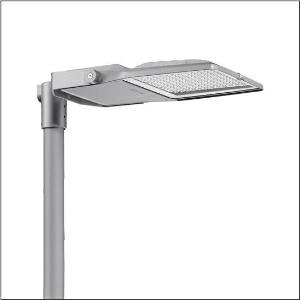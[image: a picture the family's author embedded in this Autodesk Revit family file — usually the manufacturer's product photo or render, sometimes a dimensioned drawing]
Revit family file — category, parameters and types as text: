
# Revit family: floodlight_fl_21_iq_midi___pl61_5xa7782f2c3a_b633
name_source: partatom
category: Lighting Fixtures
units: mm (PartAtom-declared; Revit-internal decimal feet)

## family parameters
Cut with Voids When Loaded = No
Host = Face
Light Source = No
Part Type = Normal
Room Calculation Point = No
Round Connector Dimension = Use Diameter
Shared = No

## types (1)
- --- (1 x LED, 35100 lm, 270.2 W, 3000K)
    Apparent Load = 270 VA
    CIE Flux Codes = 33 65 98 100 100
    Color Rendering = 70
    Color Temperature = 3000K
    Default Elevation = 1800 mm
    Description = Floodlight FL 21 iQ midi, floodlight, primary light control with lens, of PMMA, primary optical cover: protective disc, of toughened safety glass, transparent, light distribution: PL61, light emission: direct distribution, installation type: surface-mounted, LED, High Power LED, rated luminous flux: 35.100lm, luminous efficacy: 130lm/W, light colour: 730, colour temperature: 3000K, control gear: ECG iQ, control: optimised constant luminous flux control (CLO 2.0), Desk-Remote (wireless, voltage-free reading and setting of iQ features in the workshop via application-optimized NFC function/RFID function), Smart-Wire, Night-Set, Temp-Guard, Auto-Match, Street-Remote, with terminal, 6-pole, mains connection: 220..240V, AC, 50/60Hz, start of lifetime: 270W, end of service life: 287W, reduction: 117W, luminaire housing, of diecast aluminium, powder-coated, Siteco® metallic grey (DB 702S), corrosivity category C5 mid according to DIN EN ISO 12944, sealing non-destructively replaceable, please order mast flange separately, mast bracket, of steel, galvanised, powder-coated, Siteco® metallic grey (DB 702S), protection rating (complete): IP66, insulation class (complete): insulation class II (safety insulation), certification: CE, ENEC, VDE, protection symbol: D, impact resistance: IK08, permissible operating ambient temperature: -40..+40°C, permissible operating ambient temperature for outdoor applications: -40..+50°C, standard: DIN EN 12944, LABS conformity tested according to VDMA 24364:2018-05, packaging unit: 1 piece

Light Distribution: PL61
    Height = 76 mm
    Lamp = 1 x LED
    Lamp Light Flux = 35100 lm
    Lamp Power = 270.2 W
    Lamp count = 1
    Length = 657 mm
    Luminous efficacy = 130 lm/W
    Manufacturer = Siteco
    ModVariant = No
    Model = 5XA7782F2C3A
    Number of Poles = 1
    OnlyDefault = Yes
    Power Factor = 1
    Product Name = Floodlight FL 21 iQ midi | PL61
    Product group = floodlight | pylon annexe
    ProductGroupID = 6200
    Protection Class = Protection class II
    Protection Degree = IP 66
    RLX_Detail_Level = 1
    RLX_Emergency_Light_Flux = 0 lm
    RLX_Emergency_Type = 0
    RLX_Emergency_Type_DB = No
    RlxData = <blob elided: 153433 chars, md5=419d809f>
    Socket = socket
    Standby Power = 0 W
    System Light Flux = 35100 lm
    System Power = 270 W
    Type Comments = factory setting: luminous flux: 100 % | dim-lin: 254 | 620 mA
    Type Image = l_1007123.jpg
    URL = http://relux.com
    VarID = @adj_077145
    Voltage = 0 V
    Weight = 0.00 kg
    Width = 442 mm

## geometry (parser evidence)
native form markers: Blend x4, Sweep x15
no freeform markers — native parametric forms only
